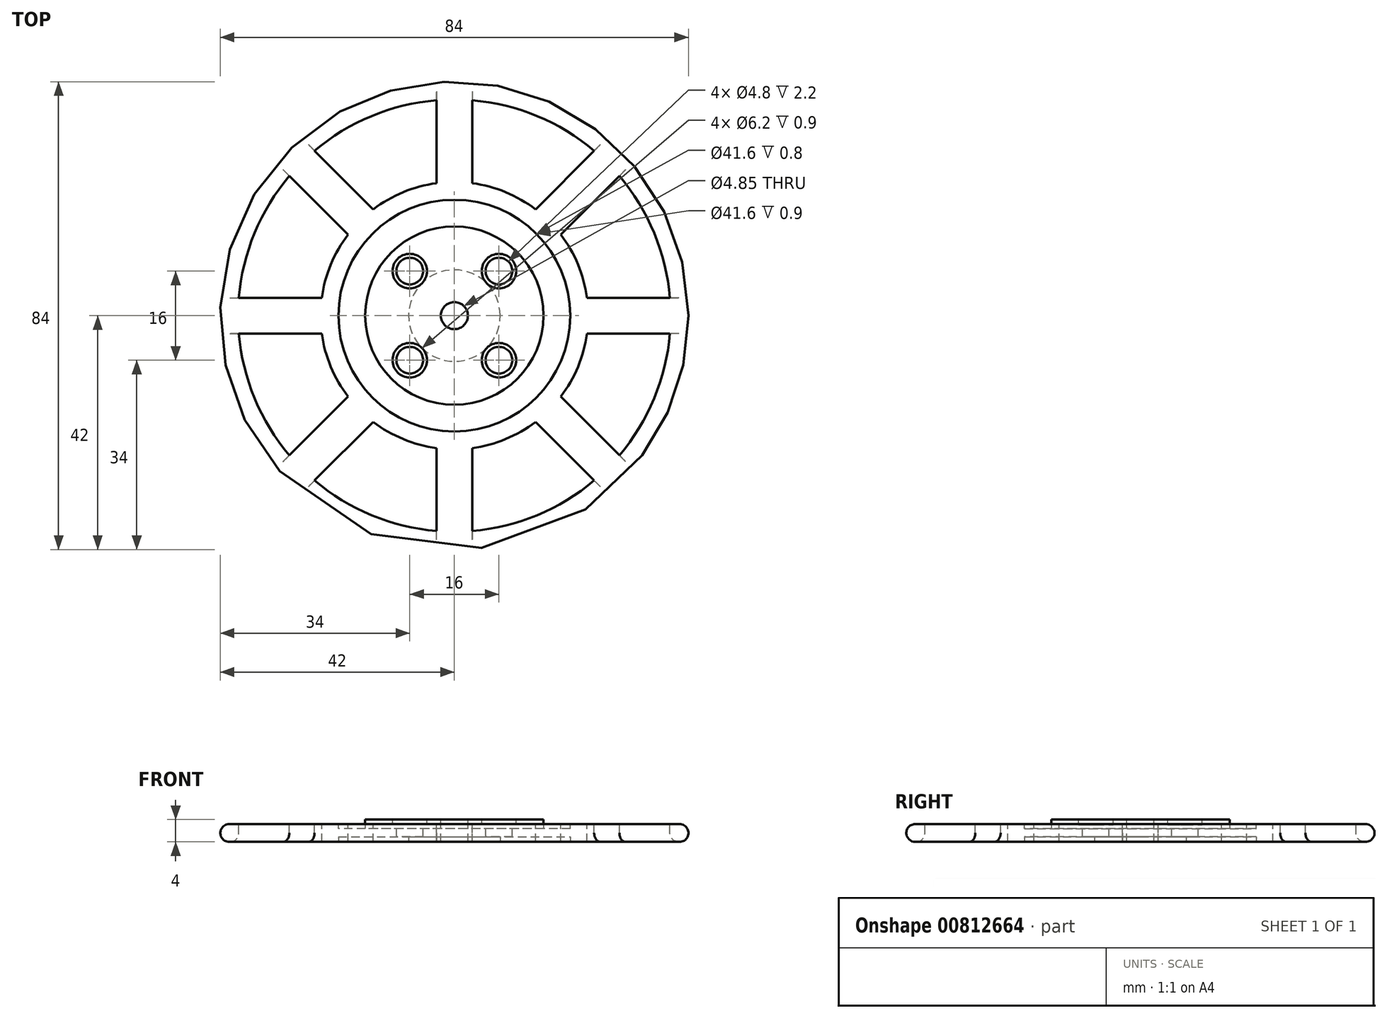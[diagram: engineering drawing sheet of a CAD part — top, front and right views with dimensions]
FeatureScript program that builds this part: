
annotation { "Feature Type Name" : "Feature", "Feature Type Description" : "" }
export const myFeature = defineFeature(function(context is Context, id is Id, definition is map)
    precondition{}
    {
        {
            var Q0;
            Q0=qCreatedBy(makeId("Top.planeOp"),FACE);
            var sketch = newSketch(context, id + "F0", { "sketchPlane" : qUnion([Q0])});
            skCircle(sketch, "E0", {"center": v(0, 0) * mm, "radius": 42 * mm});
            skSolve(sketch);
        }
        {
            var Q0;
            Q0 = qSketchRegion(id + "F0", true);
            extrude(context, id + "F1", {"entities" : qUnion([Q0]), "oppositeDirection" : true, "depth" : (9.6 / 3) * mm, "offsetDistance" : 25 * mm});
        }
        {
            var Q0;
            Q0=makeQuery(id+"F1.opExtrude","CAP_FACE",FACE,{"disambiguationData":[OSD([sQuery(id+"F0.wireOp",EDGE,"E0")])],"isStart":true});
            var sketch = newSketch(context, id + "F2", { "sketchPlane" : qUnion([Q0])});
            skCircle(sketch, "E1", {"center": v(0, 0) * mm, "radius": 38.8 * mm});
            skCircle(sketch, "E2", {"center": v(0, 0) * mm, "radius": 16 * mm});
            skSolve(sketch);
        }
        {
            var Q0;
            Q0=makeQuery(id+"F2.imprint","IMPRINT",FACE,{"disambiguationData":[TD([[makeQuery(id+"F2.imprint","IMPRINT",EDGE,{"derivedFrom":sQuery(id+"F2.wireOp",EDGE,"E2")}),1.0]])]});
            extrude(context, id + "F3", {"entities" : qUnion([Q0]), "operationType" : NewBodyOperationType.ADD, "depth" : (4 - 3.2) * mm, "offsetDistance" : 25 * mm});
        }
        {
            var Q0;
            Q0=makeQuery(id+"F1.opExtrude","CAP_FACE",FACE,{"disambiguationData":[OSD([sQuery(id+"F0.wireOp",EDGE,"E0")])],"isStart":true});
            var sketch = newSketch(context, id + "F4", { "sketchPlane" : qUnion([Q0])});
            skCircle(sketch, "E3", {"center": v(0, 0) * mm, "radius": 38.8 * mm});
            skCircle(sketch, "E4", {"center": v(0, 0) * mm, "radius": 24 * mm});
            skLineSegment(sketch, "E5", {"start": v(0, 0) * mm, "end": v(0, 67.01) * mm, "construction": true});
            skLineSegment(sketch, "E6", {"start": v(0, 0) * mm, "end": v(-53.27, 53.27) * mm, "construction": true});
            skLineSegment(sketch, "E7", {"start": v(-3.2, 38.67) * mm, "end": v(-3.2, 23.79) * mm});
            skLineSegment(sketch, "E8", {"start": v(-25.08, 29.6) * mm, "end": v(-14.56, 19.08) * mm});
            skLineSegment(sketch, "E9.1.0", {"start": v(-29.6, 25.08) * mm, "end": v(-19.08, 14.56) * mm});
            skLineSegment(sketch, "E9.1.1", {"start": v(-38.67, 3.2) * mm, "end": v(-23.79, 3.2) * mm});
            skLineSegment(sketch, "E9.2.0", {"start": v(-38.67, -3.2) * mm, "end": v(-23.79, -3.2) * mm});
            skLineSegment(sketch, "E9.2.1", {"start": v(-29.6, -25.08) * mm, "end": v(-19.08, -14.56) * mm});
            skLineSegment(sketch, "E9.3.0", {"start": v(-25.08, -29.6) * mm, "end": v(-14.56, -19.08) * mm});
            skLineSegment(sketch, "E9.3.1", {"start": v(-3.2, -38.67) * mm, "end": v(-3.2, -23.79) * mm});
            skLineSegment(sketch, "E9.4.0", {"start": v(3.2, -38.67) * mm, "end": v(3.2, -23.79) * mm});
            skLineSegment(sketch, "E9.4.1", {"start": v(25.08, -29.6) * mm, "end": v(14.56, -19.08) * mm});
            skLineSegment(sketch, "E9.5.0", {"start": v(29.6, -25.08) * mm, "end": v(19.08, -14.56) * mm});
            skLineSegment(sketch, "E9.5.1", {"start": v(38.67, -3.2) * mm, "end": v(23.79, -3.2) * mm});
            skLineSegment(sketch, "E9.6.0", {"start": v(38.67, 3.2) * mm, "end": v(23.79, 3.2) * mm});
            skLineSegment(sketch, "E9.6.1", {"start": v(29.6, 25.08) * mm, "end": v(19.08, 14.56) * mm});
            skLineSegment(sketch, "E9.7.0", {"start": v(25.08, 29.6) * mm, "end": v(14.56, 19.08) * mm});
            skLineSegment(sketch, "E9.7.1", {"start": v(3.2, 38.67) * mm, "end": v(3.2, 23.79) * mm});
            skSolve(sketch);
        }
        {
            var Q0;
            {var subQ0=sQuery(id+"F4.wireOp",EDGE,"E9.7.0");Q0=makeQuery(id+"F4.imprint","IMPRINT",FACE,{"disambiguationData":[TD([[makeQuery(id+"F4.imprint","IMPRINT",EDGE,{"derivedFrom":subQ0}),-1.0]])]});}
            var Q1;
            {var subQ0=sQuery(id+"F4.wireOp",EDGE,"E7");Q1=makeQuery(id+"F4.imprint","IMPRINT",FACE,{"disambiguationData":[TD([[makeQuery(id+"F4.imprint","IMPRINT",EDGE,{"derivedFrom":subQ0}),-1.0]])]});}
            var Q2;
            {var subQ0=sQuery(id+"F4.wireOp",EDGE,"E9.1.0");Q2=makeQuery(id+"F4.imprint","IMPRINT",FACE,{"disambiguationData":[TD([[makeQuery(id+"F4.imprint","IMPRINT",EDGE,{"derivedFrom":subQ0}),-1.0]])]});}
            var Q3;
            {var subQ0=sQuery(id+"F4.wireOp",EDGE,"E9.2.0");Q3=makeQuery(id+"F4.imprint","IMPRINT",FACE,{"disambiguationData":[TD([[makeQuery(id+"F4.imprint","IMPRINT",EDGE,{"derivedFrom":subQ0}),-1.0]])]});}
            var Q4;
            {var subQ0=sQuery(id+"F4.wireOp",EDGE,"E9.3.0");Q4=makeQuery(id+"F4.imprint","IMPRINT",FACE,{"disambiguationData":[TD([[makeQuery(id+"F4.imprint","IMPRINT",EDGE,{"derivedFrom":subQ0}),-1.0]])]});}
            var Q5;
            {var subQ0=sQuery(id+"F4.wireOp",EDGE,"E9.4.0");Q5=makeQuery(id+"F4.imprint","IMPRINT",FACE,{"disambiguationData":[TD([[makeQuery(id+"F4.imprint","IMPRINT",EDGE,{"derivedFrom":subQ0}),-1.0]])]});}
            var Q6;
            {var subQ0=sQuery(id+"F4.wireOp",EDGE,"E9.5.0");Q6=makeQuery(id+"F4.imprint","IMPRINT",FACE,{"disambiguationData":[TD([[makeQuery(id+"F4.imprint","IMPRINT",EDGE,{"derivedFrom":subQ0}),-1.0]])]});}
            var Q7;
            {var subQ0=sQuery(id+"F4.wireOp",EDGE,"E9.6.0");Q7=makeQuery(id+"F4.imprint","IMPRINT",FACE,{"disambiguationData":[TD([[makeQuery(id+"F4.imprint","IMPRINT",EDGE,{"derivedFrom":subQ0}),-1.0]])]});}
            extrude(context, id + "F5", {"entities" : qUnion([Q0, Q1, Q2, Q3, Q4, Q5, Q6, Q7]), "operationType" : NewBodyOperationType.REMOVE, "endBound" : BoundingType.THROUGH_ALL, "oppositeDirection" : true, "depth" : 25 * mm, "offsetDistance" : 25 * mm});
        }
        {
            var Q0;
            Q0=makeQuery(id+"F1.opExtrude","CAP_FACE",FACE,{"disambiguationData":[OSD([sQuery(id+"F0.wireOp",EDGE,"E0")])],"isStart":true});
            var sketch = newSketch(context, id + "F6", { "sketchPlane" : qUnion([Q0])});
            skCircle(sketch, "E10", {"center": v(0, 0) * mm, "radius": 20.8 * mm});
            skSolve(sketch);
        }
        {
            var Q0;
            Q0=makeQuery(id+"F6.imprint","IMPRINT",FACE,{"disambiguationData":[TD([[makeQuery(id+"F6.imprint","IMPRINT",EDGE,{"derivedFrom":sQuery(id+"F6.wireOp",EDGE,"E10")}),1.0]])]});
            extrude(context, id + "F7", {"entities" : qUnion([Q0]), "operationType" : NewBodyOperationType.REMOVE, "oppositeDirection" : true, "depth" : 0.8 * mm, "offsetDistance" : 25 * mm});
        }
        {
            var Q0;
            Q0=makeQuery(id+"F3.opExtrude","CAP_FACE",FACE,{"disambiguationData":[OSD([sQuery(id+"F2.wireOp",EDGE,"E2")])],"isStart":false});
            var sketch = newSketch(context, id + "F8", { "sketchPlane" : qUnion([Q0])});
            skPoint(sketch, "E11", {"position": v(-8, 8) * mm});
            skLineSegment(sketch, "E12", {"start": v(0, 0) * mm, "end": v(0, 45.65) * mm, "construction": true});
            skLineSegment(sketch, "E13", {"start": v(0, 0) * mm, "end": v(-42.92, 0) * mm, "construction": true});
            skCircle(sketch, "E14", {"center": v(-8, 8) * mm, "radius": 2.4 * mm});
            skCircle(sketch, "E15.0.1.0", {"center": v(-8, -8) * mm, "radius": 2.4 * mm});
            skCircle(sketch, "E15.1.0.0", {"center": v(8, 8) * mm, "radius": 2.4 * mm});
            skCircle(sketch, "E15.1.1.0", {"center": v(8, -8) * mm, "radius": 2.4 * mm});
            skLineSegment(sketch, "E15.direction1", {"start": v(-8, 8) * mm, "end": v(8, 8) * mm, "construction": true});
            skLineSegment(sketch, "E15.direction2", {"start": v(-8, 8) * mm, "end": v(-8, -8) * mm, "construction": true});
            skCircle(sketch, "E16", {"center": v(0, 0) * mm, "radius": 2.43 * mm});
            skSolve(sketch);
        }
        {
            var Q0;
            {var subQ0=sQuery(id+"F8.wireOp",EDGE,"E15.0.1.0");var subQ1=makeQuery(id+"F3.opExtrude","CAP_EDGE",EDGE,{"disambiguationData":[OSD([sQuery(id+"F2.wireOp",EDGE,"E2")])],"isStart":false});var subQ2=makeQuery(id+"F8.imprint","INTERSECT",VERTEX,{"disambiguationData":[OD(0.0)],"derivedFrom":[subQ1,subQ0]});Q0=makeQuery(id+"F8.imprint","IMPRINT",FACE,{"disambiguationData":[TD([[makeQuery(id+"F8.imprint","IMPRINT",EDGE,{"disambiguationData":[TD([[subQ2,-1.0]])],"derivedFrom":subQ0}),1.0]])]});}
            var Q1;
            {var subQ0=sQuery(id+"F8.wireOp",EDGE,"E15.1.0.0");var subQ1=makeQuery(id+"F3.opExtrude","CAP_EDGE",EDGE,{"disambiguationData":[OSD([sQuery(id+"F2.wireOp",EDGE,"E2")])],"isStart":false});var subQ2=makeQuery(id+"F8.imprint","INTERSECT",VERTEX,{"disambiguationData":[OD(0.0)],"derivedFrom":[subQ1,subQ0]});Q1=makeQuery(id+"F8.imprint","IMPRINT",FACE,{"disambiguationData":[TD([[makeQuery(id+"F8.imprint","IMPRINT",EDGE,{"disambiguationData":[TD([[subQ2,1.0]])],"derivedFrom":subQ0}),1.0]])]});}
            var Q2;
            {var subQ0=sQuery(id+"F8.wireOp",EDGE,"E14");var subQ1=makeQuery(id+"F3.opExtrude","CAP_EDGE",EDGE,{"disambiguationData":[OSD([sQuery(id+"F2.wireOp",EDGE,"E2")])],"isStart":false});var subQ2=makeQuery(id+"F8.imprint","INTERSECT",VERTEX,{"disambiguationData":[OD(0.0)],"derivedFrom":[subQ1,subQ0]});Q2=makeQuery(id+"F8.imprint","IMPRINT",FACE,{"disambiguationData":[TD([[makeQuery(id+"F8.imprint","IMPRINT",EDGE,{"disambiguationData":[TD([[subQ2,1.0]])],"derivedFrom":subQ0}),1.0]])]});}
            var Q3;
            {var subQ0=sQuery(id+"F8.wireOp",EDGE,"E15.1.1.0");var subQ1=makeQuery(id+"F3.opExtrude","CAP_EDGE",EDGE,{"disambiguationData":[OSD([sQuery(id+"F2.wireOp",EDGE,"E2")])],"isStart":false});var subQ2=makeQuery(id+"F8.imprint","INTERSECT",VERTEX,{"disambiguationData":[OD(0.0)],"derivedFrom":[subQ1,subQ0]});Q3=makeQuery(id+"F8.imprint","IMPRINT",FACE,{"disambiguationData":[TD([[makeQuery(id+"F8.imprint","IMPRINT",EDGE,{"disambiguationData":[TD([[subQ2,-1.0]])],"derivedFrom":subQ0}),1.0]])]});}
            var Q4;
            Q4=makeQuery(id+"F8.imprint","IMPRINT",FACE,{"disambiguationData":[TD([[makeQuery(id+"F8.imprint","IMPRINT",EDGE,{"derivedFrom":sQuery(id+"F8.wireOp",EDGE,"E16")}),1.0]])]});
            var Q5;
            Q5=makeQuery(id+"F7.boolean.opBoolean","COPY",FACE,{"derivedFrom":makeQuery(id+"F7.opExtrude","CAP_FACE",FACE,{"disambiguationData":[OSD([sQuery(id+"F2.wireOp",EDGE,"E2"),sQuery(id+"F6.wireOp",EDGE,"E10")])],"isStart":false})});
            extrude(context, id + "F9", {"entities" : qUnion([Q0, Q1, Q2, Q3, Q4]), "operationType" : NewBodyOperationType.REMOVE, "endBound" : BoundingType.THROUGH_ALL, "oppositeDirection" : true, "depth" : 25 * mm, "endBoundEntityFace" : qUnion([Q5]), "offsetDistance" : 25 * mm});
        }
        {
            var Q0;
            Q0=makeQuery(id+"F3.opExtrude","CAP_FACE",FACE,{"disambiguationData":[OSD([sQuery(id+"F2.wireOp",EDGE,"E2")])],"isStart":false});
            var sketch = newSketch(context, id + "F10", { "sketchPlane" : qUnion([Q0])});
            skCircle(sketch, "E17", {"center": v(-8, 8) * mm, "radius": 3.1 * mm});
            skCircle(sketch, "E18.0.1.0", {"center": v(-8, -8) * mm, "radius": 3.1 * mm});
            skCircle(sketch, "E18.1.0.0", {"center": v(8, 8) * mm, "radius": 3.1 * mm});
            skCircle(sketch, "E18.1.1.0", {"center": v(8, -8) * mm, "radius": 3.1 * mm});
            skLineSegment(sketch, "E18.direction1", {"start": v(-8, 8) * mm, "end": v(8, 8) * mm, "construction": true});
            skLineSegment(sketch, "E18.direction2", {"start": v(-8, 8) * mm, "end": v(-8, -8) * mm, "construction": true});
            skSolve(sketch);
        }
        {
            var Q0;
            Q0=makeQuery(id+"F10.imprint","IMPRINT",FACE,{"disambiguationData":[TD([[makeQuery(id+"F10.imprint","IMPRINT",EDGE,{"derivedFrom":sQuery(id+"F10.wireOp",EDGE,"E18.1.0.0")}),1.0]])]});
            var Q1;
            Q1=makeQuery(id+"F10.imprint","IMPRINT",FACE,{"disambiguationData":[TD([[makeQuery(id+"F10.imprint","IMPRINT",EDGE,{"derivedFrom":sQuery(id+"F10.wireOp",EDGE,"E17")}),1.0]])]});
            var Q2;
            Q2=makeQuery(id+"F10.imprint","IMPRINT",FACE,{"disambiguationData":[TD([[makeQuery(id+"F10.imprint","IMPRINT",EDGE,{"derivedFrom":sQuery(id+"F10.wireOp",EDGE,"E18.0.1.0")}),1.0]])]});
            var Q3;
            Q3=makeQuery(id+"F10.imprint","IMPRINT",FACE,{"disambiguationData":[TD([[makeQuery(id+"F10.imprint","IMPRINT",EDGE,{"derivedFrom":sQuery(id+"F10.wireOp",EDGE,"E18.1.1.0")}),1.0]])]});
            extrude(context, id + "F11", {"entities" : qUnion([Q0, Q1, Q2, Q3]), "operationType" : NewBodyOperationType.REMOVE, "oppositeDirection" : true, "depth" : 0.9 * mm, "offsetDistance" : 25 * mm});
        }
        {
            var Q0;
            Q0=makeQuery(id+"F1.opExtrude","CAP_FACE",FACE,{"disambiguationData":[OSD([sQuery(id+"F0.wireOp",EDGE,"E0")])],"isStart":false});
            var sketch = newSketch(context, id + "F12", { "sketchPlane" : qUnion([Q0])});
            skCircle(sketch, "E19", {"center": v(0, 0) * mm, "radius": 20.8 * mm});
            skCircle(sketch, "E20", {"center": v(0, 0) * mm, "radius": 8.21 * mm});
            skPoint(sketch, "E21", {"position": v(-8, -8) * mm});
            skSolve(sketch);
        }
        {
            var Q0;
            Q0=makeQuery(id+"F12.imprint","IMPRINT",FACE,{"disambiguationData":[TD([[makeQuery(id+"F12.imprint","IMPRINT",EDGE,{"derivedFrom":sQuery(id+"F12.wireOp",EDGE,"E19")}),1.0]])]});
            extrude(context, id + "F13", {"entities" : qUnion([Q0]), "operationType" : NewBodyOperationType.REMOVE, "oppositeDirection" : true, "depth" : 0.9 * mm, "offsetDistance" : 25 * mm});
        }
        {
            var Q0;
            Q0=makeQuery(id+"F1.opExtrude","CAP_EDGE",EDGE,{"disambiguationData":[OSD([sQuery(id+"F0.wireOp",EDGE,"E0")])],"isStart":true});
            var Q1;
            Q1=makeQuery(id+"F1.opExtrude","CAP_EDGE",EDGE,{"disambiguationData":[OSD([sQuery(id+"F0.wireOp",EDGE,"E0")])],"isStart":false});
            var Q2;
            {var subQ0=sQuery(id+"F4.wireOp",EDGE,"E3");Q2=makeQuery(id+"F5.boolean.opBoolean","INTERSECT",EDGE,{"derivedFrom":[makeQuery(id+"F1.opExtrude","CAP_FACE",FACE,{"disambiguationData":[OSD([sQuery(id+"F0.wireOp",EDGE,"E0")])],"isStart":false}),makeQuery(id+"F5.opExtrude","SWEPT_FACE",FACE,{"disambiguationData":[OSD([subQ0]),TDD([makeQuery(id+"F4.imprint","IMPRINT",EDGE,{"disambiguationData":[TD([[makeQuery(id+"F4.imprint","INTERSECT",VERTEX,{"derivedFrom":[subQ0,sQuery(id+"F4.wireOp",EDGE,"E9.7.0")]}),-1.0]])],"derivedFrom":subQ0})])]})]});}
            var Q3;
            {var subQ0=sQuery(id+"F4.wireOp",EDGE,"E3");Q3=makeQuery(id+"F5.boolean.opBoolean","INTERSECT",EDGE,{"derivedFrom":[makeQuery(id+"F1.opExtrude","CAP_FACE",FACE,{"disambiguationData":[OSD([sQuery(id+"F0.wireOp",EDGE,"E0")])],"isStart":false}),makeQuery(id+"F5.opExtrude","SWEPT_FACE",FACE,{"disambiguationData":[OSD([subQ0]),TDD([makeQuery(id+"F4.imprint","IMPRINT",EDGE,{"disambiguationData":[TD([[makeQuery(id+"F4.imprint","INTERSECT",VERTEX,{"derivedFrom":[subQ0,sQuery(id+"F4.wireOp",EDGE,"E9.6.0")]}),-1.0]])],"derivedFrom":subQ0})])]})]});}
            var Q4;
            {var subQ0=sQuery(id+"F4.wireOp",EDGE,"E3");Q4=makeQuery(id+"F5.boolean.opBoolean","INTERSECT",EDGE,{"derivedFrom":[makeQuery(id+"F1.opExtrude","CAP_FACE",FACE,{"disambiguationData":[OSD([sQuery(id+"F0.wireOp",EDGE,"E0")])],"isStart":false}),makeQuery(id+"F5.opExtrude","SWEPT_FACE",FACE,{"disambiguationData":[OSD([subQ0]),TDD([makeQuery(id+"F4.imprint","IMPRINT",EDGE,{"disambiguationData":[TD([[makeQuery(id+"F4.imprint","INTERSECT",VERTEX,{"derivedFrom":[subQ0,sQuery(id+"F4.wireOp",EDGE,"E9.5.0")]}),-1.0]])],"derivedFrom":subQ0})])]})]});}
            var Q5;
            {var subQ0=sQuery(id+"F4.wireOp",EDGE,"E3");Q5=makeQuery(id+"F5.boolean.opBoolean","INTERSECT",EDGE,{"derivedFrom":[makeQuery(id+"F1.opExtrude","CAP_FACE",FACE,{"disambiguationData":[OSD([sQuery(id+"F0.wireOp",EDGE,"E0")])],"isStart":false}),makeQuery(id+"F5.opExtrude","SWEPT_FACE",FACE,{"disambiguationData":[OSD([subQ0]),TDD([makeQuery(id+"F4.imprint","IMPRINT",EDGE,{"disambiguationData":[TD([[makeQuery(id+"F4.imprint","INTERSECT",VERTEX,{"derivedFrom":[subQ0,sQuery(id+"F4.wireOp",EDGE,"E9.4.0")]}),-1.0]])],"derivedFrom":subQ0})])]})]});}
            var Q6;
            {var subQ0=sQuery(id+"F4.wireOp",EDGE,"E3");Q6=makeQuery(id+"F5.boolean.opBoolean","INTERSECT",EDGE,{"derivedFrom":[makeQuery(id+"F1.opExtrude","CAP_FACE",FACE,{"disambiguationData":[OSD([sQuery(id+"F0.wireOp",EDGE,"E0")])],"isStart":false}),makeQuery(id+"F5.opExtrude","SWEPT_FACE",FACE,{"disambiguationData":[OSD([subQ0]),TDD([makeQuery(id+"F4.imprint","IMPRINT",EDGE,{"disambiguationData":[TD([[makeQuery(id+"F4.imprint","INTERSECT",VERTEX,{"derivedFrom":[subQ0,sQuery(id+"F4.wireOp",EDGE,"E9.2.0")]}),-1.0]])],"derivedFrom":subQ0})])]})]});}
            var Q7;
            {var subQ0=sQuery(id+"F4.wireOp",EDGE,"E3");Q7=makeQuery(id+"F5.boolean.opBoolean","INTERSECT",EDGE,{"derivedFrom":[makeQuery(id+"F1.opExtrude","CAP_FACE",FACE,{"disambiguationData":[OSD([sQuery(id+"F0.wireOp",EDGE,"E0")])],"isStart":false}),makeQuery(id+"F5.opExtrude","SWEPT_FACE",FACE,{"disambiguationData":[OSD([subQ0]),TDD([makeQuery(id+"F4.imprint","IMPRINT",EDGE,{"disambiguationData":[TD([[makeQuery(id+"F4.imprint","INTERSECT",VERTEX,{"derivedFrom":[subQ0,sQuery(id+"F4.wireOp",EDGE,"E9.1.0")]}),-1.0]])],"derivedFrom":subQ0})])]})]});}
            var Q8;
            {var subQ0=sQuery(id+"F4.wireOp",EDGE,"E3");Q8=makeQuery(id+"F5.boolean.opBoolean","INTERSECT",EDGE,{"derivedFrom":[makeQuery(id+"F1.opExtrude","CAP_FACE",FACE,{"disambiguationData":[OSD([sQuery(id+"F0.wireOp",EDGE,"E0")])],"isStart":false}),makeQuery(id+"F5.opExtrude","SWEPT_FACE",FACE,{"disambiguationData":[OSD([subQ0]),TDD([makeQuery(id+"F4.imprint","IMPRINT",EDGE,{"disambiguationData":[TD([[makeQuery(id+"F4.imprint","INTERSECT",VERTEX,{"derivedFrom":[subQ0,sQuery(id+"F4.wireOp",EDGE,"E7")]}),-1.0]])],"derivedFrom":subQ0})])]})]});}
            var Q9;
            {var subQ0=sQuery(id+"F4.wireOp",EDGE,"E3");Q9=makeQuery(id+"F5.boolean.opBoolean","INTERSECT",EDGE,{"derivedFrom":[makeQuery(id+"F1.opExtrude","CAP_FACE",FACE,{"disambiguationData":[OSD([sQuery(id+"F0.wireOp",EDGE,"E0")])],"isStart":false}),makeQuery(id+"F5.opExtrude","SWEPT_FACE",FACE,{"disambiguationData":[OSD([subQ0]),TDD([makeQuery(id+"F4.imprint","IMPRINT",EDGE,{"disambiguationData":[TD([[makeQuery(id+"F4.imprint","INTERSECT",VERTEX,{"derivedFrom":[subQ0,sQuery(id+"F4.wireOp",EDGE,"E9.3.0")]}),-1.0]])],"derivedFrom":subQ0})])]})]});}
            fillet(context, id + "F14", {"entities" : qUnion([Q0, Q1, Q2, Q3, Q4, Q5, Q6, Q7, Q8, Q9]), "radius" : (3.2 / 2) * mm, "tangentPropagation" : true, "allowEdgeOverflow" : false});
        }
    });
